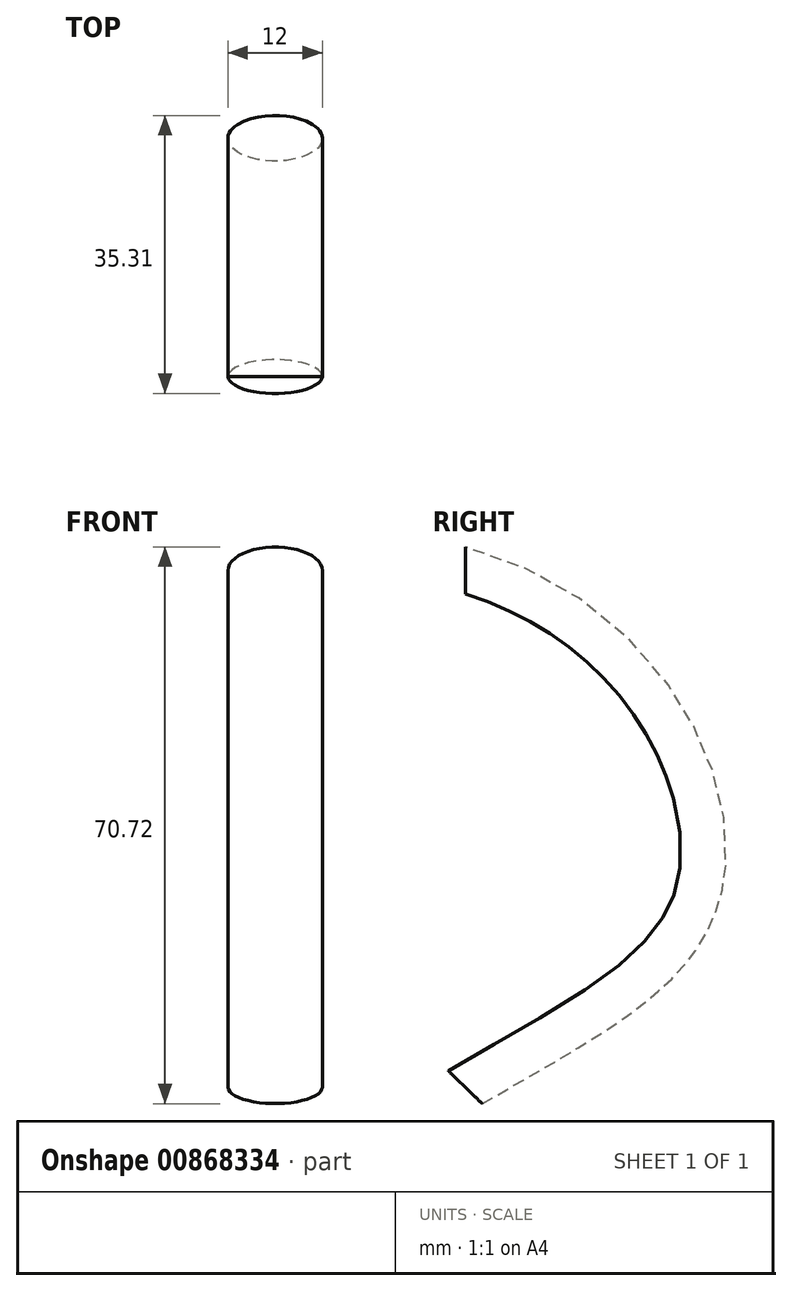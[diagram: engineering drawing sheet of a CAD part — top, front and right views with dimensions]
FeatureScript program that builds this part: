
annotation { "Feature Type Name" : "Feature", "Feature Type Description" : "" }
export const myFeature = defineFeature(function(context is Context, id is Id, definition is map)
    precondition{}
    {
        {
            var Q0;
            Q0=qCreatedBy(makeId("Front.planeOp"),FACE);
            var sketch = newSketch(context, id + "F0", { "sketchPlane" : qUnion([Q0])});
            skLineSegment(sketch, "E0", {"start": v(0, 38.83) * mm, "end": v(0, -26.67) * mm});
            skSolve(sketch);
        }
        {
            var Q0;
            Q0=qCreatedBy(makeId("Right.planeOp"),FACE);
            var sketch = newSketch(context, id + "F1", { "sketchPlane" : qUnion([Q0])});
            skFitSpline(sketch, "E1", {"points": [v(0, 38.95) * mm, v(30, 0) * mm, v(0, -26.68) * mm], "startDerivative": vector(125.27, -35.19) * mm, "endDerivative": vector(-103.73, -60.3) * mm});
            skSolve(sketch);
        }
        {
            var Q0;
            Q0=qCreatedBy(makeId("Front.planeOp"),FACE);
            var sketch = newSketch(context, id + "F2", { "sketchPlane" : qUnion([Q0])});
            skEllipse(sketch, "E2", {"center": v(0, 38.95) * mm, "majorRadius": 6 * mm, "minorRadius": 3 * mm, "majorAxis": v(1, 0)});
            skSolve(sketch);
        }
        {
            var Q0;
            Q0=makeQuery(id+"F2.imprint","IMPRINT",FACE,{"disambiguationData":[TD([[makeQuery(id+"F2.imprint","IMPRINT",EDGE,{"derivedFrom":sQuery(id+"F2.wireOp",EDGE,"E2")}),1.0]])]});
            var Q1;
            Q1=sQuery(id+"F1.wireOp",EDGE,"E1");
            sweep(context, id + "F3", {"profiles" : qUnion([Q0]), "path" : qUnion([Q1])});
        }
    });
